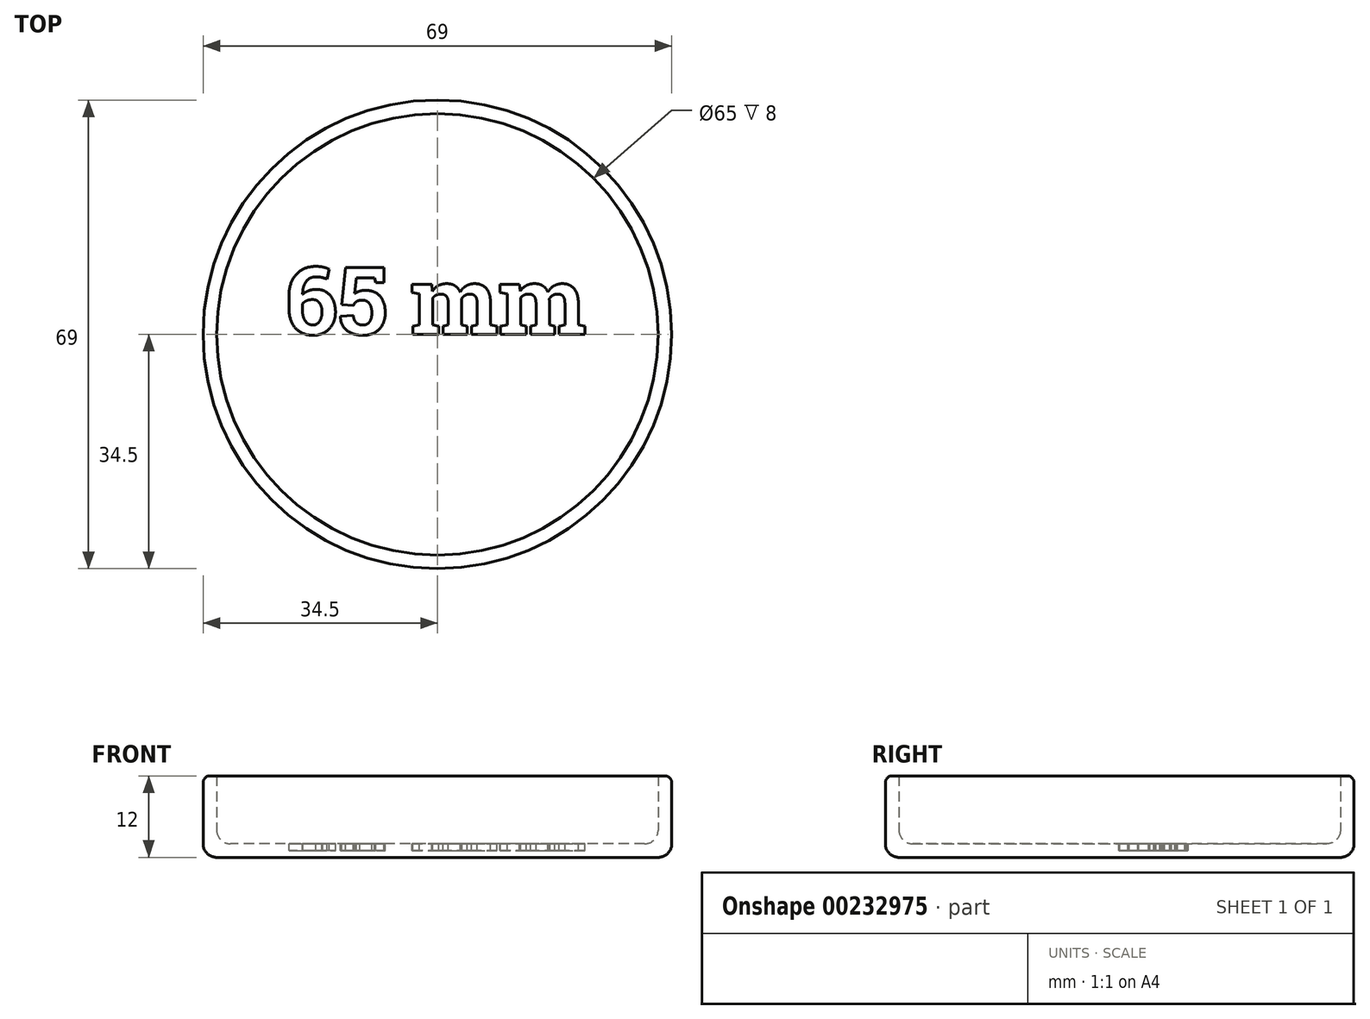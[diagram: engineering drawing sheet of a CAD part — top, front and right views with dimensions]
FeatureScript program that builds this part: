
annotation { "Feature Type Name" : "Feature", "Feature Type Description" : "" }
export const myFeature = defineFeature(function(context is Context, id is Id, definition is map)
    precondition{}
    {
        {
            assignVariable(context, id + "F0", {"name" : "Kappen_staerke", "anyValue" : 2 * mm});
        }
        {
            assignVariable(context, id + "F1", {"name" : "Kappen_hoehe", "anyValue" : 10 * mm});
        }
        {
            var Q0;
            Q0=qCreatedBy(makeId("Top.planeOp"),FACE);
            var sketch = newSketch(context, id + "F2", { "sketchPlane" : qUnion([Q0])});
            skCircle(sketch, "E0", {"center": v(0, 0) * mm, "radius": 32.5 * mm});
            skSolve(sketch);
        }
        {
            var Q0;
            Q0=makeQuery(id+"F2.imprint","IMPRINT",FACE,{"disambiguationData":[TD([[makeQuery(id+"F2.imprint","IMPRINT",EDGE,{"derivedFrom":sQuery(id+"F2.wireOp",EDGE,"E0")}),1.0]])]});
            extrude(context, id + "F3", {"entities" : qUnion([Q0]), "depth" : getVariable(context, 'Kappen_hoehe')});
        }
        {
            var Q0;
            Q0=makeQuery(id+"F3.opExtrude","CAP_FACE",FACE,{"disambiguationData":[OSD([sQuery(id+"F2.wireOp",EDGE,"E0")])],"isStart":false});
            shell(context, id + "F4", {"entities" : qUnion([Q0]), "thickness" : getVariable(context, 'Kappen_staerke'), "oppositeDirection" : true});
        }
        {
            var Q0;
            Q0=makeQuery(id+"F3.opExtrude","CAP_EDGE",EDGE,{"disambiguationData":[OSD([sQuery(id+"F2.wireOp",EDGE,"E0")])],"isStart":true});
            fillet(context, id + "F5", {"entities" : qUnion([Q0]), "radius" : 2 * mm, "tangentPropagation" : true, "allowEdgeOverflow" : false});
        }
        {
            var Q0;
            {var subQ0=sQuery(id+"F2.wireOp",EDGE,"E0");Q0=makeQuery(id+"F4.opShell","OFFSET_EDGE",EDGE,{"disambiguationData":[OSD([subQ0]),TDD([makeQuery(id+"F3.opExtrude","CAP_EDGE",EDGE,{"disambiguationData":[OSD([subQ0])],"isStart":true})])]});}
            fillet(context, id + "F6", {"entities" : qUnion([Q0]), "radius" : 2 * mm, "tangentPropagation" : true, "allowEdgeOverflow" : false});
        }
        {
            var Q0;
            Q0=makeQuery(id+"F3.opExtrude","CAP_EDGE",EDGE,{"disambiguationData":[OSD([sQuery(id+"F2.wireOp",EDGE,"E0")])],"isStart":false});
            fillet(context, id + "F7", {"entities" : qUnion([Q0]), "radius" : 1 * mm, "tangentPropagation" : true, "allowEdgeOverflow" : false});
        }
        {
            var Q0;
            {var subQ0=sQuery(id+"F2.wireOp",EDGE,"E0");Q0=makeQuery(id+"F4.opShell","OFFSET_FACE",FACE,{"disambiguationData":[OSD([subQ0]),TDD([makeQuery(id+"F3.opExtrude","CAP_FACE",FACE,{"disambiguationData":[OSD([subQ0])],"isStart":true})])]});}
            var sketch = newSketch(context, id + "F8", { "sketchPlane" : qUnion([Q0])});
            skText(sketch, "E1", { "text": "65 mm", "fontName": "RobotoSlab-Bold.ttf"});
            const initialGuessF8  = {"E1": [-0.02248, 0, 1, 0, 0.01]};
            skSetInitialGuess(sketch, initialGuessF8);
            skSolve(sketch);
        }
        {
            var Q0;
            Q0=qSketchRegion(id+"F8",true);
            extrude(context, id + "F9", {"entities" : qUnion([Q0]), "operationType" : NewBodyOperationType.REMOVE, "oppositeDirection" : true, "depth" : 1 * mm});
        }
    });
